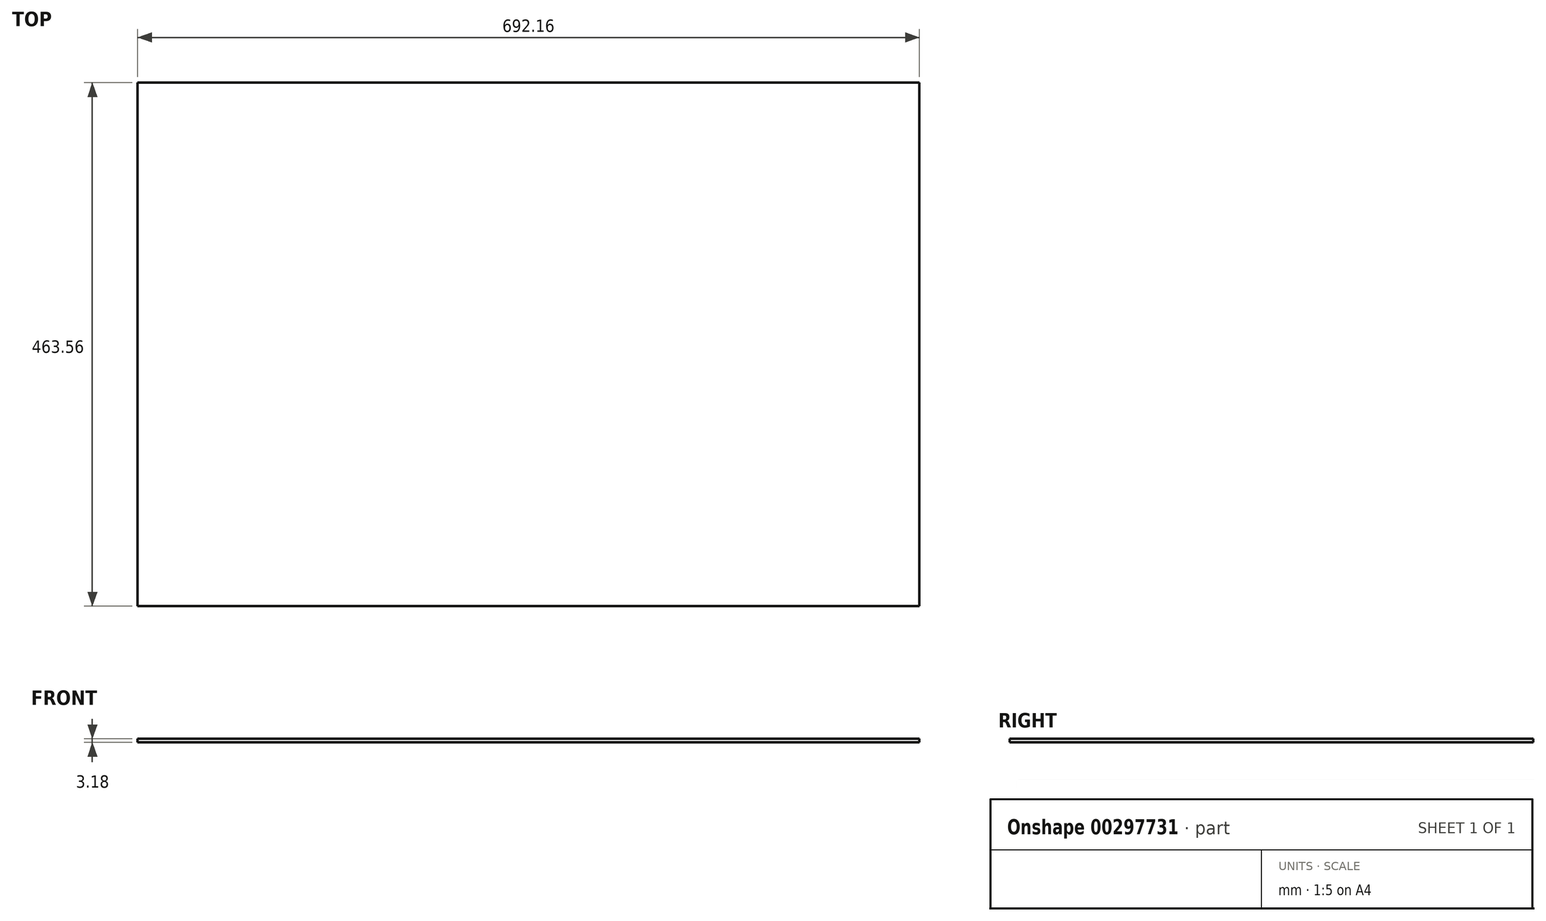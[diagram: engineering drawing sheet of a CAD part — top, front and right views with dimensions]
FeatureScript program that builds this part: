
annotation { "Feature Type Name" : "Feature", "Feature Type Description" : "" }
export const myFeature = defineFeature(function(context is Context, id is Id, definition is map)
    precondition{}
    {
        {
            var Q0;
            Q0=qCreatedBy(makeId("Top.planeOp"),FACE);
            var sketch = newSketch(context, id + "F0", { "sketchPlane" : qUnion([Q0])});
            skLineSegment(sketch, "E0.bottom", {"start": v(346.08, -231.77) * mm, "end": v(-346.08, -231.78) * mm});
            skLineSegment(sketch, "E0.top", {"start": v(346.08, 231.78) * mm, "end": v(-346.08, 231.77) * mm});
            skLineSegment(sketch, "E0.left", {"start": v(346.08, -231.78) * mm, "end": v(346.08, 231.78) * mm});
            skLineSegment(sketch, "E0.right", {"start": v(-346.08, -231.78) * mm, "end": v(-346.08, 231.78) * mm});
            skPoint(sketch, "E0.middle", {"position": v(0, 0) * mm});
            skSolve(sketch);
        }
        {
            var Q0;
            Q0 = qSketchRegion(id + "F0", true);
            extrude(context, id + "F1", {"entities" : qUnion([Q0]), "endBound" : BoundingType.SYMMETRIC, "depth" : 3.17 * mm});
        }
    });
